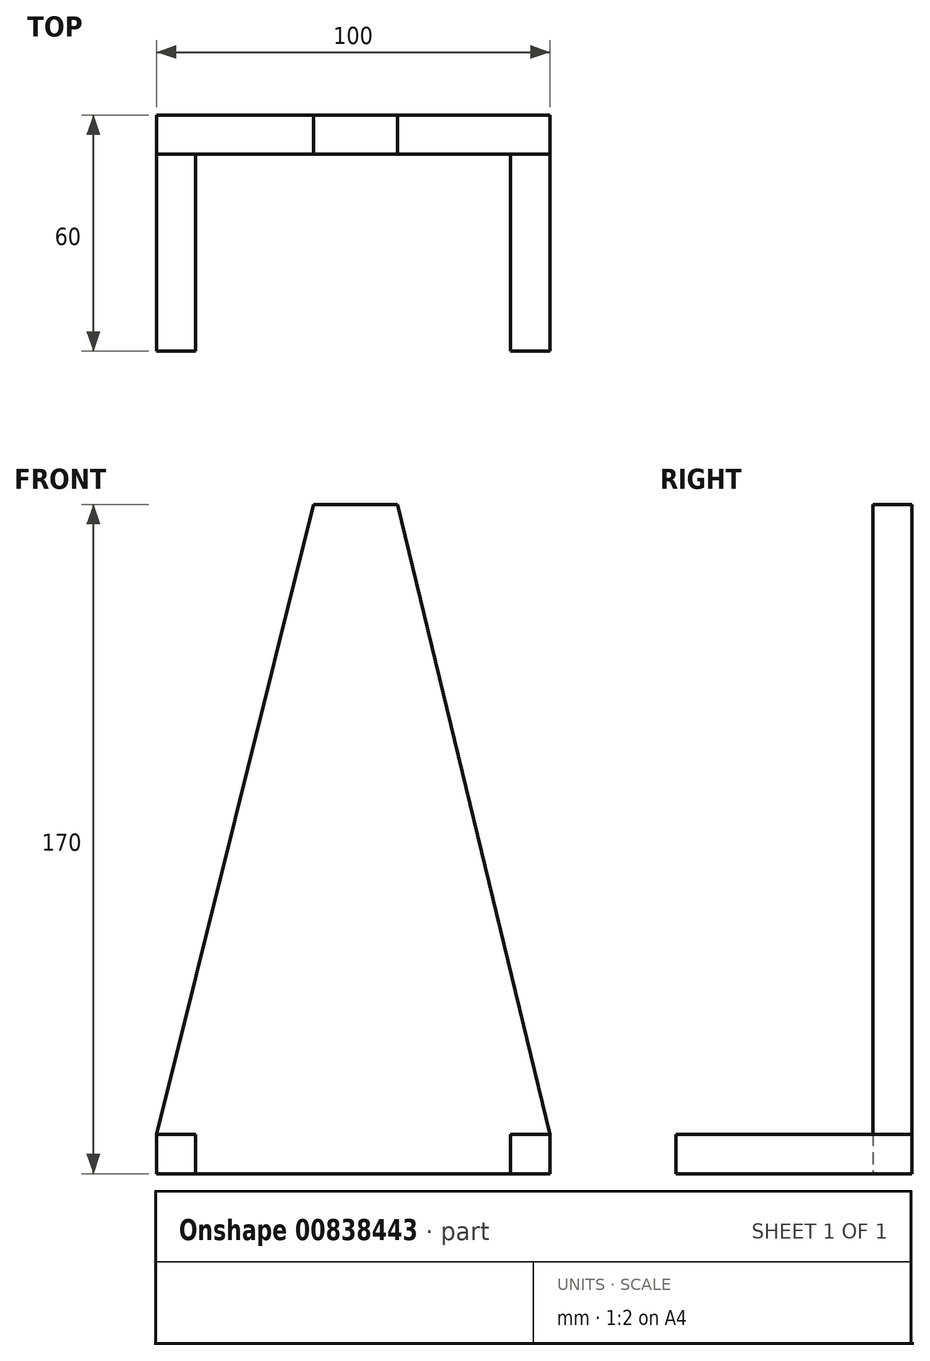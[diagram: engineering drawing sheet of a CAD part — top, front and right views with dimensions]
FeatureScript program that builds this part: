
annotation { "Feature Type Name" : "Feature", "Feature Type Description" : "" }
export const myFeature = defineFeature(function(context is Context, id is Id, definition is map)
    precondition{}
    {
        {
            var Q0;
            Q0=qCreatedBy(makeId("Top.planeOp"),FACE);
            var sketch = newSketch(context, id + "F0", { "sketchPlane" : qUnion([Q0])});
            skLineSegment(sketch, "E0.bottom", {"start": v(40, 25) * mm, "end": v(-40, 25) * mm});
            skLineSegment(sketch, "E0.left", {"start": v(40, 25) * mm, "end": v(40, -25) * mm});
            skLineSegment(sketch, "E0.right", {"start": v(-40, 25) * mm, "end": v(-40, -25) * mm});
            skPoint(sketch, "E0.middle", {"position": v(0, 0) * mm});
            skLineSegment(sketch, "E1.bottom", {"start": v(50, 35) * mm, "end": v(-50, 35) * mm});
            skLineSegment(sketch, "E1.left", {"start": v(50, 35) * mm, "end": v(50, -25) * mm});
            skLineSegment(sketch, "E1.right", {"start": v(-50, 35) * mm, "end": v(-50, -25) * mm});
            skLineSegment(sketch, "E2", {"start": v(-40, -25) * mm, "end": v(-50, -25) * mm});
            skLineSegment(sketch, "E3", {"start": v(40, -25) * mm, "end": v(50, -25) * mm});
            skPoint(sketch, "E1.top.end.orphan", {"position": v(-50, -35) * mm});
            skPoint(sketch, "E4.orphan", {"position": v(50, -35) * mm});
            skLineSegment(sketch, "E5", {"start": v(-40, 25) * mm, "end": v(-50, 25) * mm});
            skLineSegment(sketch, "E6", {"start": v(40, 25) * mm, "end": v(50, 25) * mm});
            skSolve(sketch);
        }
        {
            var Q0;
            Q0=makeQuery(id+"F0.imprint","IMPRINT",FACE,{"disambiguationData":[TD([[makeQuery(id+"F0.imprint","IMPRINT",EDGE,{"derivedFrom":sQuery(id+"F0.wireOp",EDGE,"E0.right")}),-1.0]])]});
            var Q1;
            Q1=makeQuery(id+"F0.imprint","IMPRINT",FACE,{"disambiguationData":[TD([[makeQuery(id+"F0.imprint","IMPRINT",EDGE,{"derivedFrom":sQuery(id+"F0.wireOp",EDGE,"E0.left")}),1.0]])]});
            extrude(context, id + "F1", {"entities" : qUnion([Q0, Q1]), "depth" : 10 * mm, "offsetDistance" : 25.4 * mm});
        }
        {
            var Q0;
            Q0=makeQuery(id+"F1.opExtrude","CAP_FACE",FACE,{"disambiguationData":[OSD([sQuery(id+"F0.wireOp",EDGE,"E0.right"),sQuery(id+"F0.wireOp",EDGE,"E1.right"),sQuery(id+"F0.wireOp",EDGE,"E2"),sQuery(id+"F0.wireOp",EDGE,"E5")])],"isStart":false});
            cPlane(context, id + "F2", {"entities" : qUnion([Q0]), "cplaneType" : CPlaneType.OFFSET, "offset" : 160 * mm, "width" : 152.4 * mm, "height" : 152.4 * mm});
        }
        {
            var Q0;
            Q0=qCreatedBy(id+"F2.planeOp",FACE);
            var sketch = newSketch(context, id + "F3", { "sketchPlane" : qUnion([Q0])});
            skPoint(sketch, "E7.middle", {"position": v(0, 0) * mm});
            skLineSegment(sketch, "E8", {"start": v(-10, 35) * mm, "end": v(0, 35) * mm});
            skLineSegment(sketch, "E9.right", {"start": v(11.32, 35) * mm, "end": v(11.32, 25) * mm});
            skPoint(sketch, "E7.top.start.orphan", {"position": v(-50, -25) * mm});
            skPoint(sketch, "E7.right.end.orphan", {"position": v(50, -25) * mm});
            skLineSegment(sketch, "E10.bottom", {"start": v(-10, 35) * mm, "end": v(11.32, 35) * mm});
            skLineSegment(sketch, "E10.top", {"start": v(-10, 25) * mm, "end": v(11.32, 25) * mm});
            skLineSegment(sketch, "E10.left", {"start": v(-10, 35) * mm, "end": v(-10, 25) * mm});
            skLineSegment(sketch, "E11", {"start": v(0, 35) * mm, "end": v(0, 0) * mm, "construction": true});
            skSolve(sketch);
        }
        {
            var Q0;
            Q0=makeQuery(id+"F0.imprint","IMPRINT",FACE,{"disambiguationData":[TD([[makeQuery(id+"F0.imprint","IMPRINT",EDGE,{"derivedFrom":sQuery(id+"F0.wireOp",EDGE,"E0.bottom")}),-1.0]])]});
            extrude(context, id + "F4", {"entities" : qUnion([Q0]), "depth" : 10 * mm, "offsetDistance" : 25.4 * mm});
        }
        {
            var Q1;
            Q1=makeQuery(id+"F4.opExtrude","CAP_FACE",FACE,{"disambiguationData":[OSD([sQuery(id+"F0.wireOp",EDGE,"E0.bottom"),sQuery(id+"F0.wireOp",EDGE,"E1.bottom"),sQuery(id+"F0.wireOp",EDGE,"E1.left"),sQuery(id+"F0.wireOp",EDGE,"E1.right"),sQuery(id+"F0.wireOp",EDGE,"E5"),sQuery(id+"F0.wireOp",EDGE,"E6")])],"isStart":false});
            var Q2;
            Q2=makeQuery(id+"F3.imprint","IMPRINT",FACE,{"disambiguationData":[TD([[makeQuery(id+"F3.imprint","IMPRINT",EDGE,{"derivedFrom":sQuery(id+"F3.wireOp",EDGE,"E10.top")}),1.0]])]});
            loft(context, id + "F5", {"operationType" : NewBodyOperationType.ADD, "sheetProfilesArray" : [{ "sheetProfileEntities" : qUnion([Q1]) }, { "sheetProfileEntities" : qUnion([Q2]) }]});
        }
    });
